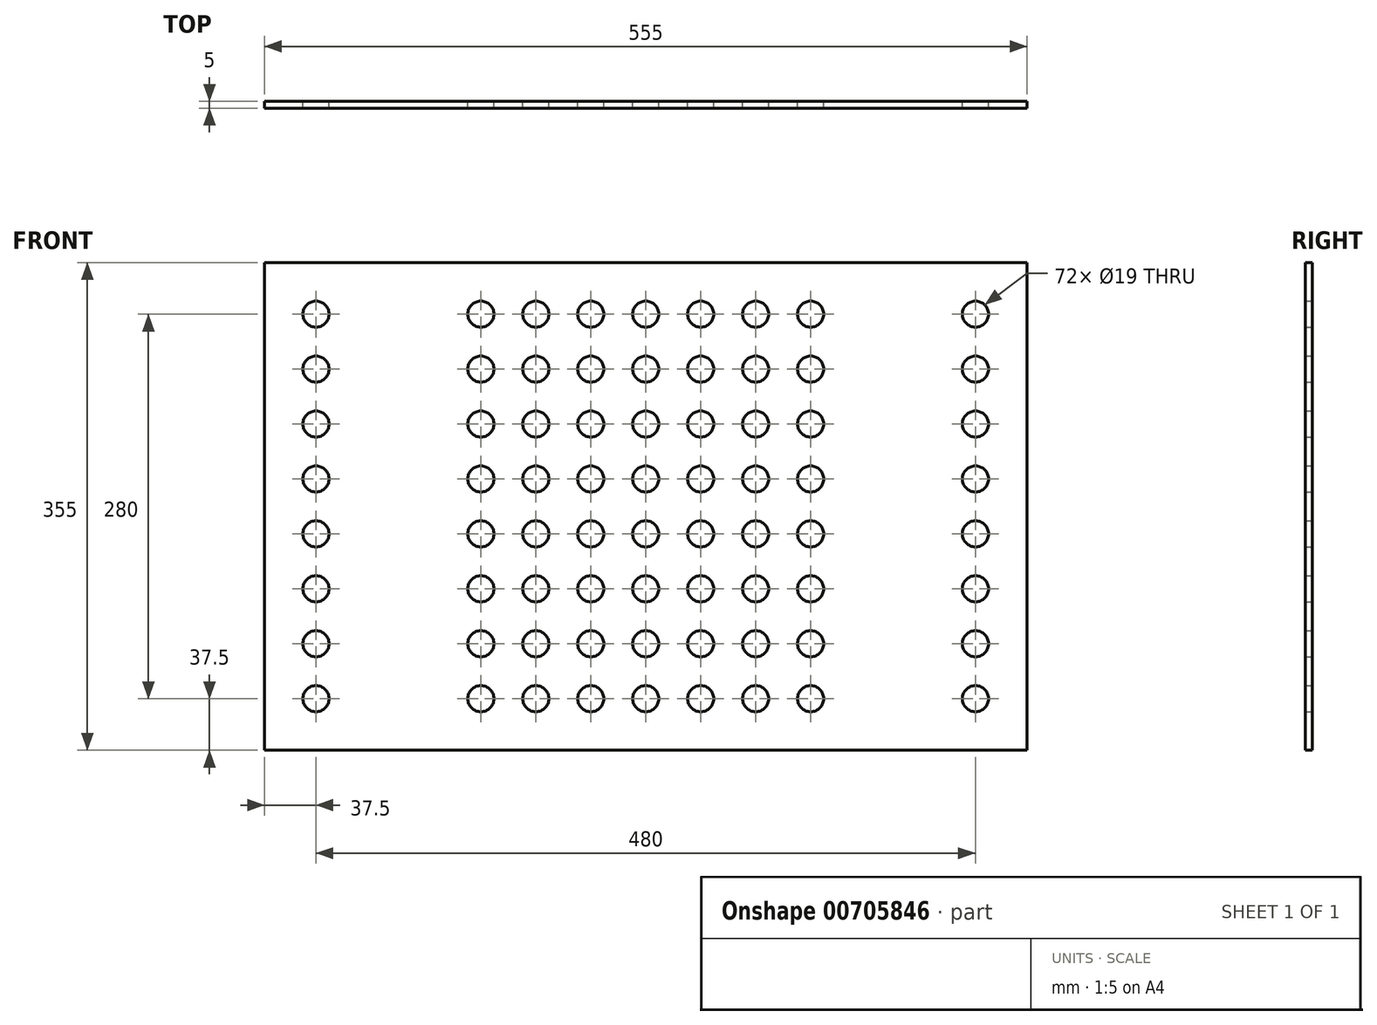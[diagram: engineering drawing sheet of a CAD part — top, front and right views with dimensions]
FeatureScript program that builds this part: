
annotation { "Feature Type Name" : "Feature", "Feature Type Description" : "" }
export const myFeature = defineFeature(function(context is Context, id is Id, definition is map)
    precondition{}
    {
        {
            var Q0;
            Q0=qCreatedBy(makeId("Front.planeOp"),FACE);
            var sketch = newSketch(context, id + "F0", { "sketchPlane" : qUnion([Q0])});
            skLineSegment(sketch, "E0.bottom", {"start": v(277.5, 177.5) * mm, "end": v(-277.5, 177.5) * mm});
            skLineSegment(sketch, "E0.top", {"start": v(277.5, -177.5) * mm, "end": v(-277.5, -177.5) * mm});
            skLineSegment(sketch, "E0.left", {"start": v(277.5, 177.5) * mm, "end": v(277.5, -177.5) * mm});
            skLineSegment(sketch, "E0.right", {"start": v(-277.5, 177.5) * mm, "end": v(-277.5, -177.5) * mm});
            skPoint(sketch, "E0.middle", {"position": v(0, 0) * mm});
            skSolve(sketch);
        }
        {
            var Q0;
            Q0 = qSketchRegion(id + "F0", true);
            extrude(context, id + "F1", {"entities" : qUnion([Q0]), "endBound" : BoundingType.SYMMETRIC, "depth" : 5 * mm, "offsetDistance" : 25 * mm});
        }
        {
            var Q0;
            Q0=qCreatedBy(makeId("Front.planeOp"),FACE);
            var sketch = newSketch(context, id + "F2", { "sketchPlane" : qUnion([Q0])});
            skCircle(sketch, "E1", {"center": v(-240, -140) * mm, "radius": 9.5 * mm});
            skCircle(sketch, "E2.0.1.0", {"center": v(-240, -100) * mm, "radius": 9.5 * mm});
            skCircle(sketch, "E2.0.2.0", {"center": v(-240, -60) * mm, "radius": 9.5 * mm});
            skCircle(sketch, "E2.3.0.0", {"center": v(-120, -140) * mm, "radius": 9.5 * mm});
            skCircle(sketch, "E2.3.1.0", {"center": v(-120, -100) * mm, "radius": 9.5 * mm});
            skCircle(sketch, "E2.3.2.0", {"center": v(-120, -60) * mm, "radius": 9.5 * mm});
            skLineSegment(sketch, "E2.direction1", {"start": v(-63.49, -43.5) * mm, "end": v(-33.49, -43.5) * mm, "construction": true});
            skLineSegment(sketch, "E2.direction2", {"start": v(-63.49, -43.5) * mm, "end": v(-63.49, -23.5) * mm, "construction": true});
            skCircle(sketch, "E3.0.4.0", {"center": v(-80, -140) * mm, "radius": 9.5 * mm});
            skCircle(sketch, "E3.0.4.1", {"center": v(-80, -100) * mm, "radius": 9.5 * mm});
            skCircle(sketch, "E3.0.4.2", {"center": v(-80, -60) * mm, "radius": 9.5 * mm});
            skCircle(sketch, "E4.0.0.3", {"center": v(-240, -20) * mm, "radius": 9.5 * mm});
            skCircle(sketch, "E4.0.3.3", {"center": v(-120, -20) * mm, "radius": 9.5 * mm});
            skCircle(sketch, "E4.0.4.3", {"center": v(-80, -20) * mm, "radius": 9.5 * mm});
            skCircle(sketch, "E5.0.5.0", {"center": v(-40, -140) * mm, "radius": 9.5 * mm});
            skCircle(sketch, "E5.0.5.1", {"center": v(-40, -100) * mm, "radius": 9.5 * mm});
            skCircle(sketch, "E5.0.5.2", {"center": v(-40, -60) * mm, "radius": 9.5 * mm});
            skCircle(sketch, "E5.0.5.3", {"center": v(-40, -20) * mm, "radius": 9.5 * mm});
            skCircle(sketch, "E5.0.6.0", {"center": v(0, -140) * mm, "radius": 9.5 * mm});
            skCircle(sketch, "E5.0.6.1", {"center": v(0, -100) * mm, "radius": 9.5 * mm});
            skCircle(sketch, "E5.0.6.2", {"center": v(0, -60) * mm, "radius": 9.5 * mm});
            skCircle(sketch, "E5.0.6.3", {"center": v(0, -20) * mm, "radius": 9.5 * mm});
            skCircle(sketch, "E5.0.7.0", {"center": v(40, -140) * mm, "radius": 9.5 * mm});
            skCircle(sketch, "E5.0.7.1", {"center": v(40, -100) * mm, "radius": 9.5 * mm});
            skCircle(sketch, "E5.0.7.2", {"center": v(40, -60) * mm, "radius": 9.5 * mm});
            skCircle(sketch, "E5.0.7.3", {"center": v(40, -20) * mm, "radius": 9.5 * mm});
            skCircle(sketch, "E5.0.8.0", {"center": v(80, -140) * mm, "radius": 9.5 * mm});
            skCircle(sketch, "E5.0.8.1", {"center": v(80, -100) * mm, "radius": 9.5 * mm});
            skCircle(sketch, "E5.0.8.2", {"center": v(80, -60) * mm, "radius": 9.5 * mm});
            skCircle(sketch, "E5.0.8.3", {"center": v(80, -20) * mm, "radius": 9.5 * mm});
            skCircle(sketch, "E5.0.9.0", {"center": v(120, -140) * mm, "radius": 9.5 * mm});
            skCircle(sketch, "E5.0.9.1", {"center": v(120, -100) * mm, "radius": 9.5 * mm});
            skCircle(sketch, "E5.0.9.2", {"center": v(120, -60) * mm, "radius": 9.5 * mm});
            skCircle(sketch, "E5.0.9.3", {"center": v(120, -20) * mm, "radius": 9.5 * mm});
            skCircle(sketch, "E6.0.0.4", {"center": v(-240, 20) * mm, "radius": 9.5 * mm});
            skCircle(sketch, "E6.0.0.5", {"center": v(-240, 60) * mm, "radius": 9.5 * mm});
            skCircle(sketch, "E6.0.0.6", {"center": v(-240, 100) * mm, "radius": 9.5 * mm});
            skCircle(sketch, "E6.0.0.7", {"center": v(-240, 140) * mm, "radius": 9.5 * mm});
            skCircle(sketch, "E6.0.3.4", {"center": v(-120, 20) * mm, "radius": 9.5 * mm});
            skCircle(sketch, "E6.0.3.5", {"center": v(-120, 60) * mm, "radius": 9.5 * mm});
            skCircle(sketch, "E6.0.3.6", {"center": v(-120, 100) * mm, "radius": 9.5 * mm});
            skCircle(sketch, "E6.0.3.7", {"center": v(-120, 140) * mm, "radius": 9.5 * mm});
            skCircle(sketch, "E6.0.4.4", {"center": v(-80, 20) * mm, "radius": 9.5 * mm});
            skCircle(sketch, "E6.0.4.5", {"center": v(-80, 60) * mm, "radius": 9.5 * mm});
            skCircle(sketch, "E6.0.4.6", {"center": v(-80, 100) * mm, "radius": 9.5 * mm});
            skCircle(sketch, "E6.0.4.7", {"center": v(-80, 140) * mm, "radius": 9.5 * mm});
            skCircle(sketch, "E6.0.5.4", {"center": v(-40, 20) * mm, "radius": 9.5 * mm});
            skCircle(sketch, "E6.0.5.5", {"center": v(-40, 60) * mm, "radius": 9.5 * mm});
            skCircle(sketch, "E6.0.5.6", {"center": v(-40, 100) * mm, "radius": 9.5 * mm});
            skCircle(sketch, "E6.0.5.7", {"center": v(-40, 140) * mm, "radius": 9.5 * mm});
            skCircle(sketch, "E6.0.6.4", {"center": v(0, 20) * mm, "radius": 9.5 * mm});
            skCircle(sketch, "E6.0.6.5", {"center": v(0, 60) * mm, "radius": 9.5 * mm});
            skCircle(sketch, "E6.0.6.6", {"center": v(0, 100) * mm, "radius": 9.5 * mm});
            skCircle(sketch, "E6.0.6.7", {"center": v(0, 140) * mm, "radius": 9.5 * mm});
            skCircle(sketch, "E6.0.7.4", {"center": v(40, 20) * mm, "radius": 9.5 * mm});
            skCircle(sketch, "E6.0.7.5", {"center": v(40, 60) * mm, "radius": 9.5 * mm});
            skCircle(sketch, "E6.0.7.6", {"center": v(40, 100) * mm, "radius": 9.5 * mm});
            skCircle(sketch, "E6.0.7.7", {"center": v(40, 140) * mm, "radius": 9.5 * mm});
            skCircle(sketch, "E6.0.8.4", {"center": v(80, 20) * mm, "radius": 9.5 * mm});
            skCircle(sketch, "E6.0.8.5", {"center": v(80, 60) * mm, "radius": 9.5 * mm});
            skCircle(sketch, "E6.0.8.6", {"center": v(80, 100) * mm, "radius": 9.5 * mm});
            skCircle(sketch, "E6.0.8.7", {"center": v(80, 140) * mm, "radius": 9.5 * mm});
            skCircle(sketch, "E6.0.9.4", {"center": v(120, 20) * mm, "radius": 9.5 * mm});
            skCircle(sketch, "E6.0.9.5", {"center": v(120, 60) * mm, "radius": 9.5 * mm});
            skCircle(sketch, "E6.0.9.6", {"center": v(120, 100) * mm, "radius": 9.5 * mm});
            skCircle(sketch, "E6.0.9.7", {"center": v(120, 140) * mm, "radius": 9.5 * mm});
            skLineSegment(sketch, "E7", {"start": v(-240, 177.5) * mm, "end": v(-240, 140) * mm, "construction": true});
            skLineSegment(sketch, "E8", {"start": v(-240, -140) * mm, "end": v(-240, -177.5) * mm, "construction": true});
            skCircle(sketch, "E9.0.12.0", {"center": v(240, -140) * mm, "radius": 9.5 * mm});
            skCircle(sketch, "E9.0.12.1", {"center": v(240, -100) * mm, "radius": 9.5 * mm});
            skCircle(sketch, "E9.0.12.2", {"center": v(240, -60) * mm, "radius": 9.5 * mm});
            skCircle(sketch, "E9.0.12.3", {"center": v(240, -20) * mm, "radius": 9.5 * mm});
            skCircle(sketch, "E9.0.12.4", {"center": v(240, 20) * mm, "radius": 9.5 * mm});
            skCircle(sketch, "E9.0.12.5", {"center": v(240, 60) * mm, "radius": 9.5 * mm});
            skCircle(sketch, "E9.0.12.6", {"center": v(240, 100) * mm, "radius": 9.5 * mm});
            skCircle(sketch, "E9.0.12.7", {"center": v(240, 140) * mm, "radius": 9.5 * mm});
            skLineSegment(sketch, "E10", {"start": v(-197.5, 177.5) * mm, "end": v(-197.5, -177.5) * mm, "construction": true});
            skLineSegment(sketch, "E11", {"start": v(157.5, 177.5) * mm, "end": v(157.5, -177.5) * mm, "construction": true});
            skLineSegment(sketch, "E12", {"start": v(-157.5, 177.5) * mm, "end": v(-157.5, -177.5) * mm, "construction": true});
            skLineSegment(sketch, "E13", {"start": v(197.5, 177.5) * mm, "end": v(197.5, -177.5) * mm, "construction": true});
            skSolve(sketch);
        }
        {
            var Q0;
            Q0 = qSketchRegion(id + "F2", true);
            extrude(context, id + "F3", {"entities" : qUnion([Q0]), "operationType" : NewBodyOperationType.REMOVE, "endBound" : BoundingType.THROUGH_ALL, "depth" : 25 * mm, "offsetDistance" : 25 * mm, "hasSecondDirection" : true, "secondDirectionBound" : SecondDirectionBoundingType.THROUGH_ALL, "secondDirectionOppositeDirection" : true, "secondDirectionDepth" : 25 * mm});
        }
    });
